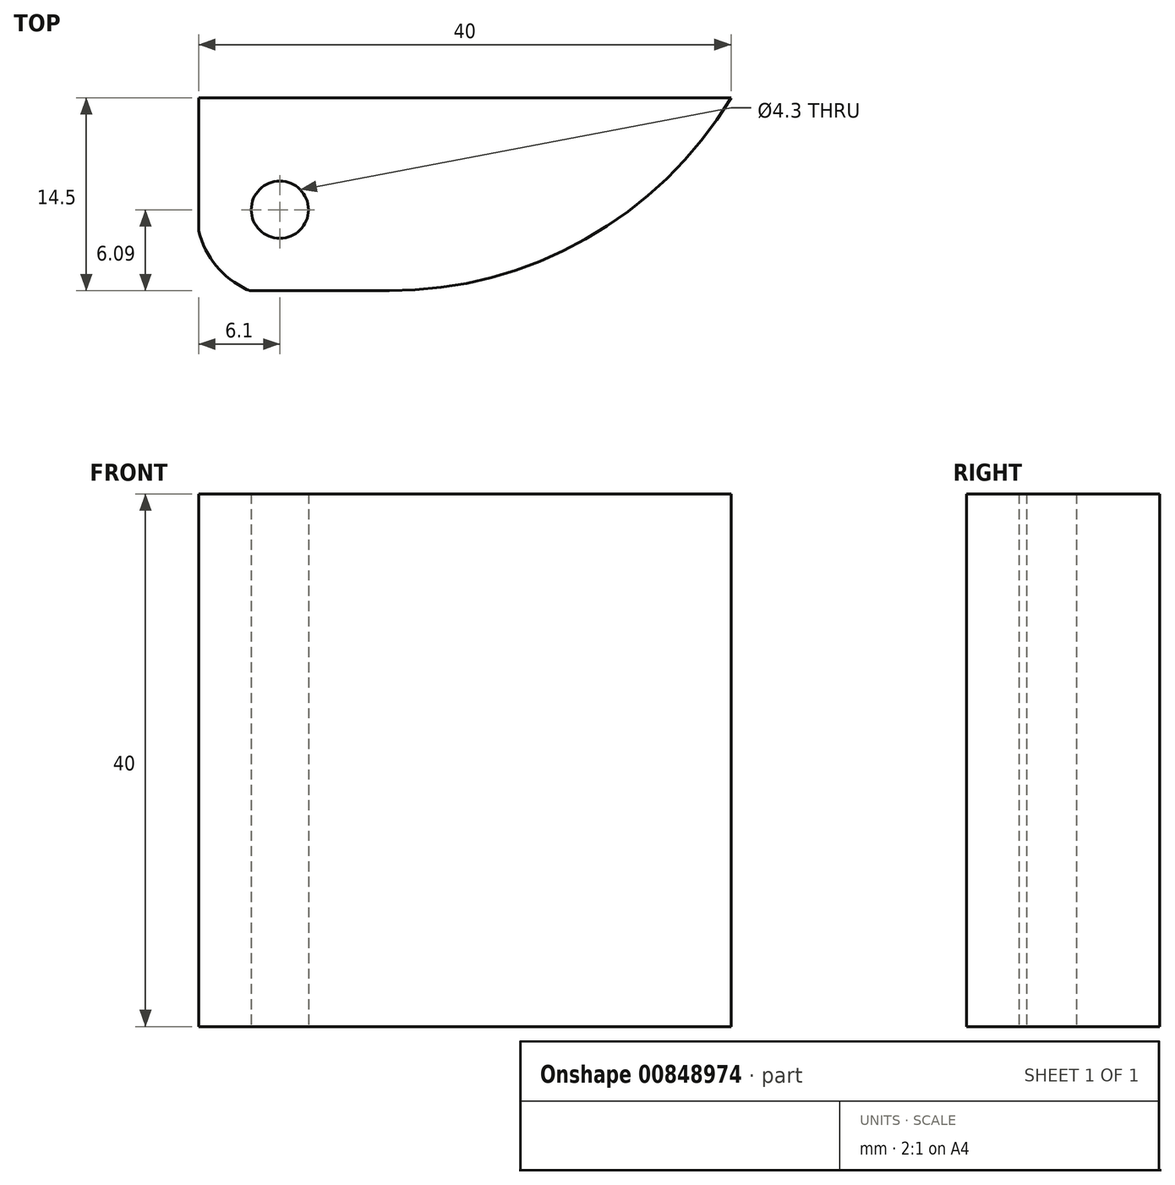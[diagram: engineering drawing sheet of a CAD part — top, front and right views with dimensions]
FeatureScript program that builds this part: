
annotation { "Feature Type Name" : "Feature", "Feature Type Description" : "" }
export const myFeature = defineFeature(function(context is Context, id is Id, definition is map)
    precondition{}
    {
        {
            var Q0;
            Q0=qCreatedBy(makeId("Top.planeOp"),FACE);
            var sketch = newSketch(context, id + "F0", { "sketchPlane" : qUnion([Q0])});
            skLineSegment(sketch, "E0.bottom", {"start": v(6.1, 8.41) * mm, "end": v(-6.1, 8.41) * mm});
            skLineSegment(sketch, "E0.left", {"start": v(6.1, 8.41) * mm, "end": v(6.1, -1.59) * mm});
            skLineSegment(sketch, "E0.right", {"start": v(-6.1, 8.41) * mm, "end": v(-6.1, -1.59) * mm});
            skArc(sketch, "E1", {"start": v(-6.1, -1.59) * mm, "mid": v(-4.7, -4.3) * mm, "end": v(-2.25, -6.09) * mm});
            skLineSegment(sketch, "E2", {"start": v(-2.25, -6.1) * mm, "end": v(0, -6.1) * mm});
            skArc(sketch, "E3.MirrorCS", {"start": v(6.1, -1.59) * mm, "mid": v(4.7, -4.3) * mm, "end": v(2.25, -6.09) * mm});
            skLineSegment(sketch, "E4.MirrorCS", {"start": v(2.25, -6.09) * mm, "end": v(0, -6.1) * mm});
            skCircle(sketch, "E5", {"center": v(0, 0) * mm, "radius": 2.15 * mm});
            skLineSegment(sketch, "E6.bottom", {"start": v(0, -6.1) * mm, "end": v(33.9, -6.1) * mm});
            skLineSegment(sketch, "E6.top", {"start": v(0, 8.41) * mm, "end": v(33.9, 8.41) * mm});
            skLineSegment(sketch, "E6.left", {"start": v(0, -6.1) * mm, "end": v(0, 8.41) * mm});
            skLineSegment(sketch, "E6.right", {"start": v(33.9, -6.1) * mm, "end": v(33.9, 8.41) * mm});
            skSolve(sketch);
        }
        {
            var Q0;
            Q0=makeQuery(id+"F0.imprint","IMPRINT",FACE,{"disambiguationData":[TD([[makeQuery(id+"F0.imprint","IMPRINT",EDGE,{"derivedFrom":sQuery(id+"F0.wireOp",EDGE,"E0.bottom")}),1.0]])]});
            var Q1;
            {var subQ7=sQuery(id+"F0.wireOp",EDGE,"E0.left");Q1=makeQuery(id+"F0.imprint","IMPRINT",FACE,{"disambiguationData":[TD([[makeQuery(id+"F0.imprint","IMPRINT",EDGE,{"derivedFrom":subQ7}),-1.0]])]});}
            var Q2;
            {var subQ4=sQuery(id+"F0.wireOp",EDGE,"E0.left");Q2=makeQuery(id+"F0.imprint","IMPRINT",FACE,{"disambiguationData":[TD([[makeQuery(id+"F0.imprint","IMPRINT",EDGE,{"derivedFrom":subQ4}),1.0]])]});}
            extrude(context, id + "F1", {"entities" : qUnion([Q0, Q1, Q2]), "depth" : 40 * mm, "offsetDistance" : 25 * mm});
        }
        {
            var Q0;
            Q0=makeQuery(id+"F1.opExtrude","SWEPT_EDGE",EDGE,{"disambiguationData":[OSD([sQuery(id+"F0.wireOp",EDGE,"E1"),sQuery(id+"F0.wireOp",EDGE,"E2")])]});
            var Q1;
            Q1=makeQuery(id+"F1.opExtrude","SWEPT_EDGE",EDGE,{"disambiguationData":[OSD([sQuery(id+"F0.wireOp",EDGE,"E3.MirrorCS"),sQuery(id+"F0.wireOp",EDGE,"E4.MirrorCS")])]});
            fillet(context, id + "F2", {"entities" : qUnion([Q0, Q1]), "radius" : 1 * mm, "tangentPropagation" : true, "allowEdgeOverflow" : false});
        }
        {
            var Q0;
            Q0=makeQuery(id+"F1.opExtrude","SWEPT_EDGE",EDGE,{"disambiguationData":[OSD([sQuery(id+"F0.wireOp",EDGE,"E6.bottom"),sQuery(id+"F0.wireOp",EDGE,"E6.right")])]});
            fillet(context, id + "F3", {"entities" : qUnion([Q0]), "radius" : 30 * mm, "tangentPropagation" : true, "allowEdgeOverflow" : false});
        }
    });
